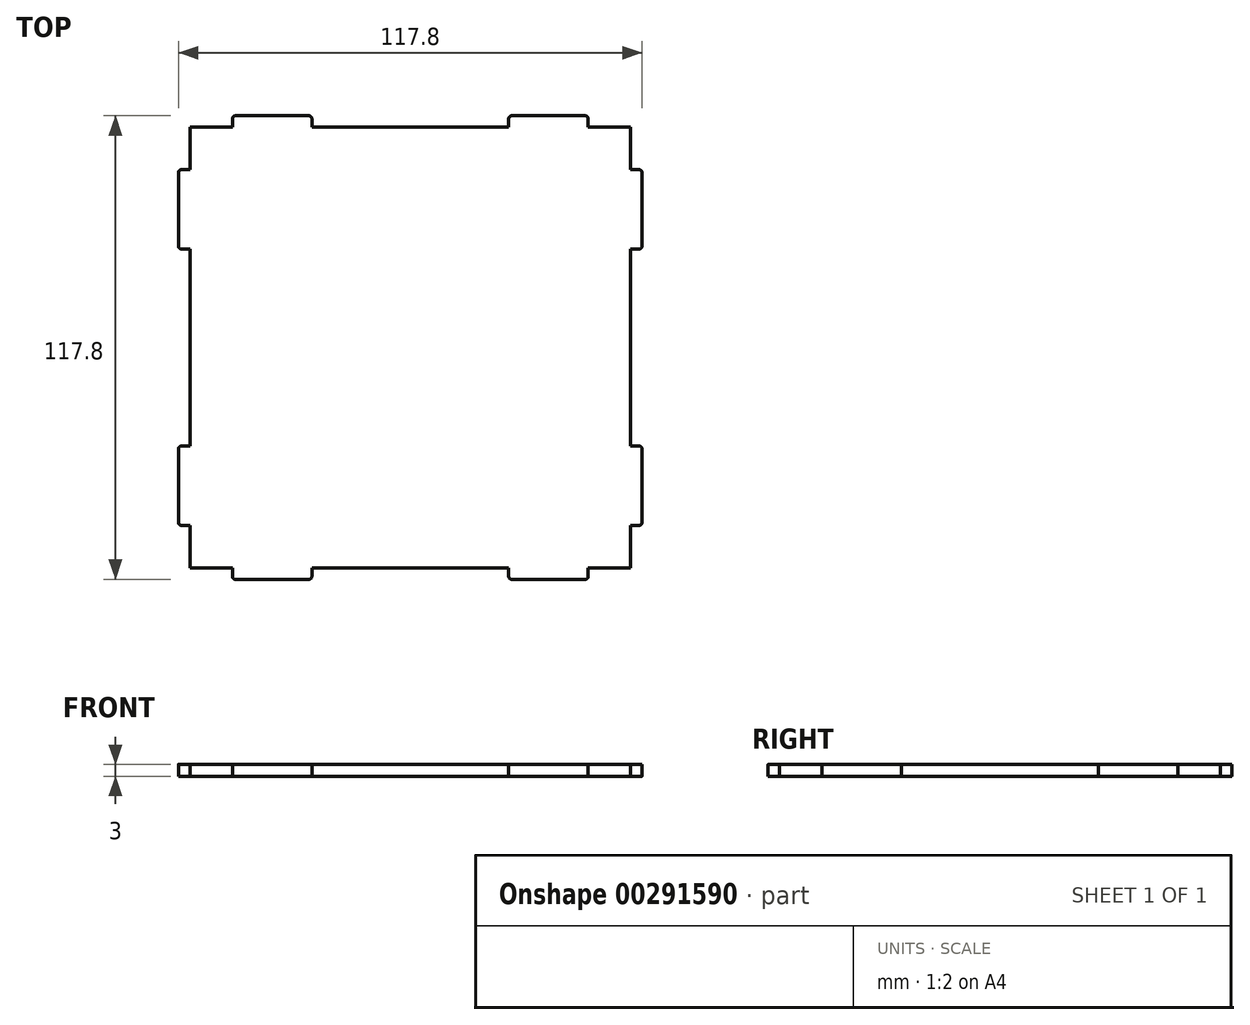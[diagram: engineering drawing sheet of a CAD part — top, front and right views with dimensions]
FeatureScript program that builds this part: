
annotation { "Feature Type Name" : "Feature", "Feature Type Description" : "" }
export const myFeature = defineFeature(function(context is Context, id is Id, definition is map)
    precondition{}
    {
        {
            var Q0;
            Q0=qCreatedBy(makeId("Top.planeOp"),FACE);
            var sketch = newSketch(context, id + "F0", { "sketchPlane" : qUnion([Q0])});
            skLineSegment(sketch, "E0", {"start": v(-45.2, 56) * mm, "end": v(-56, 56) * mm});
            skLineSegment(sketch, "E1", {"start": v(-56, 56) * mm, "end": v(-56, 45.2) * mm});
            skLineSegment(sketch, "E2", {"start": v(-56, -45.2) * mm, "end": v(-56, -56) * mm});
            skLineSegment(sketch, "E3", {"start": v(-56, -56) * mm, "end": v(-45.2, -56) * mm});
            skLineSegment(sketch, "E4", {"start": v(45.2, -56) * mm, "end": v(56, -56) * mm});
            skLineSegment(sketch, "E5", {"start": v(56, -56) * mm, "end": v(56, -45.2) * mm});
            skLineSegment(sketch, "E6", {"start": v(45.2, 56) * mm, "end": v(56, 56) * mm});
            skLineSegment(sketch, "E7", {"start": v(56, 56) * mm, "end": v(56, 45.2) * mm});
            skLineSegment(sketch, "E8", {"start": v(-56, 25) * mm, "end": v(-56, -25) * mm});
            skLineSegment(sketch, "E9", {"start": v(-25, 56) * mm, "end": v(25, 56) * mm});
            skLineSegment(sketch, "E10", {"start": v(56, 25) * mm, "end": v(56, -25) * mm});
            skLineSegment(sketch, "E11", {"start": v(-25, -56) * mm, "end": v(25, -56) * mm});
            skLineSegment(sketch, "E12", {"start": v(-56, -45.2) * mm, "end": v(-58.9, -45.2) * mm});
            skLineSegment(sketch, "E13", {"start": v(-58.9, -45.2) * mm, "end": v(-58.9, -25) * mm});
            skLineSegment(sketch, "E14", {"start": v(-58.9, -25) * mm, "end": v(-56, -25) * mm});
            skLineSegment(sketch, "E15", {"start": v(-56, 25) * mm, "end": v(-58.9, 25) * mm});
            skLineSegment(sketch, "E16", {"start": v(-58.9, 25) * mm, "end": v(-58.9, 45.2) * mm});
            skLineSegment(sketch, "E17", {"start": v(-58.9, 45.2) * mm, "end": v(-56, 45.2) * mm});
            skLineSegment(sketch, "E18", {"start": v(-45.2, 56) * mm, "end": v(-45.2, 58.9) * mm});
            skLineSegment(sketch, "E19", {"start": v(-45.2, 58.9) * mm, "end": v(-25, 58.9) * mm});
            skLineSegment(sketch, "E20", {"start": v(-25, 58.9) * mm, "end": v(-25, 56) * mm});
            skLineSegment(sketch, "E21", {"start": v(25, 56) * mm, "end": v(25, 58.9) * mm});
            skLineSegment(sketch, "E22", {"start": v(25, 58.9) * mm, "end": v(45.2, 58.9) * mm});
            skLineSegment(sketch, "E23", {"start": v(45.2, 58.9) * mm, "end": v(45.2, 56) * mm});
            skLineSegment(sketch, "E24", {"start": v(56, 45.2) * mm, "end": v(58.9, 45.2) * mm});
            skLineSegment(sketch, "E25", {"start": v(58.9, 45.2) * mm, "end": v(58.9, 25) * mm});
            skLineSegment(sketch, "E26", {"start": v(58.9, 25) * mm, "end": v(56, 25) * mm});
            skLineSegment(sketch, "E27", {"start": v(56, -25) * mm, "end": v(58.9, -25) * mm});
            skLineSegment(sketch, "E28", {"start": v(58.9, -25) * mm, "end": v(58.9, -45.2) * mm});
            skLineSegment(sketch, "E29", {"start": v(58.9, -45.2) * mm, "end": v(56, -45.2) * mm});
            skLineSegment(sketch, "E30", {"start": v(45.2, -56) * mm, "end": v(45.2, -58.9) * mm});
            skLineSegment(sketch, "E31", {"start": v(45.2, -58.9) * mm, "end": v(25, -58.9) * mm});
            skLineSegment(sketch, "E32", {"start": v(25, -58.9) * mm, "end": v(25, -56) * mm});
            skLineSegment(sketch, "E33", {"start": v(-25, -56) * mm, "end": v(-25, -58.9) * mm});
            skLineSegment(sketch, "E34", {"start": v(-25, -58.9) * mm, "end": v(-45.2, -58.9) * mm});
            skLineSegment(sketch, "E35", {"start": v(-45.2, -58.9) * mm, "end": v(-45.2, -56) * mm});
            skLineSegment(sketch, "E36", {"start": v(0, 72.71) * mm, "end": v(0, -80.58) * mm, "construction": true});
            skLineSegment(sketch, "E37", {"start": v(83.49, 0) * mm, "end": v(-105.4, 0) * mm, "construction": true});
            skSolve(sketch);
        }
        {
            var Q0;
            Q0=makeQuery(id+"F0.imprint","IMPRINT",FACE,{"disambiguationData":[TD([[makeQuery(id+"F0.imprint","IMPRINT",EDGE,{"derivedFrom":sQuery(id+"F0.wireOp",EDGE,"E0")}),1.0]])]});
            extrude(context, id + "F1", {"entities" : qUnion([Q0]), "depth" : 3 * mm});
        }
        {
            var Q0;
            Q0=makeQuery(id+"F1.opExtrude","SWEPT_EDGE",EDGE,{"disambiguationData":[OSD([sQuery(id+"F0.wireOp",EDGE,"E34"),sQuery(id+"F0.wireOp",EDGE,"E35")])]});
            var Q1;
            Q1=makeQuery(id+"F1.opExtrude","SWEPT_EDGE",EDGE,{"disambiguationData":[OSD([sQuery(id+"F0.wireOp",EDGE,"E33"),sQuery(id+"F0.wireOp",EDGE,"E34")])]});
            var Q2;
            Q2=makeQuery(id+"F1.opExtrude","SWEPT_EDGE",EDGE,{"disambiguationData":[OSD([sQuery(id+"F0.wireOp",EDGE,"E12"),sQuery(id+"F0.wireOp",EDGE,"E13")])]});
            var Q3;
            Q3=makeQuery(id+"F1.opExtrude","SWEPT_EDGE",EDGE,{"disambiguationData":[OSD([sQuery(id+"F0.wireOp",EDGE,"E15"),sQuery(id+"F0.wireOp",EDGE,"E16")])]});
            var Q4;
            Q4=makeQuery(id+"F1.opExtrude","SWEPT_EDGE",EDGE,{"disambiguationData":[OSD([sQuery(id+"F0.wireOp",EDGE,"E31"),sQuery(id+"F0.wireOp",EDGE,"E32")])]});
            var Q5;
            Q5=makeQuery(id+"F1.opExtrude","SWEPT_EDGE",EDGE,{"disambiguationData":[OSD([sQuery(id+"F0.wireOp",EDGE,"E30"),sQuery(id+"F0.wireOp",EDGE,"E31")])]});
            var Q6;
            Q6=makeQuery(id+"F1.opExtrude","SWEPT_EDGE",EDGE,{"disambiguationData":[OSD([sQuery(id+"F0.wireOp",EDGE,"E28"),sQuery(id+"F0.wireOp",EDGE,"E29")])]});
            var Q7;
            Q7=makeQuery(id+"F1.opExtrude","SWEPT_EDGE",EDGE,{"disambiguationData":[OSD([sQuery(id+"F0.wireOp",EDGE,"E25"),sQuery(id+"F0.wireOp",EDGE,"E26")])]});
            var Q8;
            Q8=makeQuery(id+"F1.opExtrude","SWEPT_EDGE",EDGE,{"disambiguationData":[OSD([sQuery(id+"F0.wireOp",EDGE,"E27"),sQuery(id+"F0.wireOp",EDGE,"E28")])]});
            var Q9;
            Q9=makeQuery(id+"F1.opExtrude","SWEPT_EDGE",EDGE,{"disambiguationData":[OSD([sQuery(id+"F0.wireOp",EDGE,"E24"),sQuery(id+"F0.wireOp",EDGE,"E25")])]});
            var Q10;
            Q10=makeQuery(id+"F1.opExtrude","SWEPT_EDGE",EDGE,{"disambiguationData":[OSD([sQuery(id+"F0.wireOp",EDGE,"E22"),sQuery(id+"F0.wireOp",EDGE,"E23")])]});
            var Q11;
            Q11=makeQuery(id+"F1.opExtrude","SWEPT_EDGE",EDGE,{"disambiguationData":[OSD([sQuery(id+"F0.wireOp",EDGE,"E19"),sQuery(id+"F0.wireOp",EDGE,"E20")])]});
            var Q12;
            Q12=makeQuery(id+"F1.opExtrude","SWEPT_EDGE",EDGE,{"disambiguationData":[OSD([sQuery(id+"F0.wireOp",EDGE,"E21"),sQuery(id+"F0.wireOp",EDGE,"E22")])]});
            var Q13;
            Q13=makeQuery(id+"F1.opExtrude","SWEPT_EDGE",EDGE,{"disambiguationData":[OSD([sQuery(id+"F0.wireOp",EDGE,"E18"),sQuery(id+"F0.wireOp",EDGE,"E19")])]});
            var Q14;
            Q14=makeQuery(id+"F1.opExtrude","SWEPT_EDGE",EDGE,{"disambiguationData":[OSD([sQuery(id+"F0.wireOp",EDGE,"E16"),sQuery(id+"F0.wireOp",EDGE,"E17")])]});
            var Q15;
            Q15=makeQuery(id+"F1.opExtrude","SWEPT_EDGE",EDGE,{"disambiguationData":[OSD([sQuery(id+"F0.wireOp",EDGE,"E13"),sQuery(id+"F0.wireOp",EDGE,"E14")])]});
            fillet(context, id + "F2", {"entities" : qUnion([Q0, Q1, Q2, Q3, Q4, Q5, Q6, Q7, Q8, Q9, Q10, Q11, Q12, Q13, Q14, Q15]), "radius" : 0.8 * mm, "tangentPropagation" : true, "allowEdgeOverflow" : false});
        }
    });
